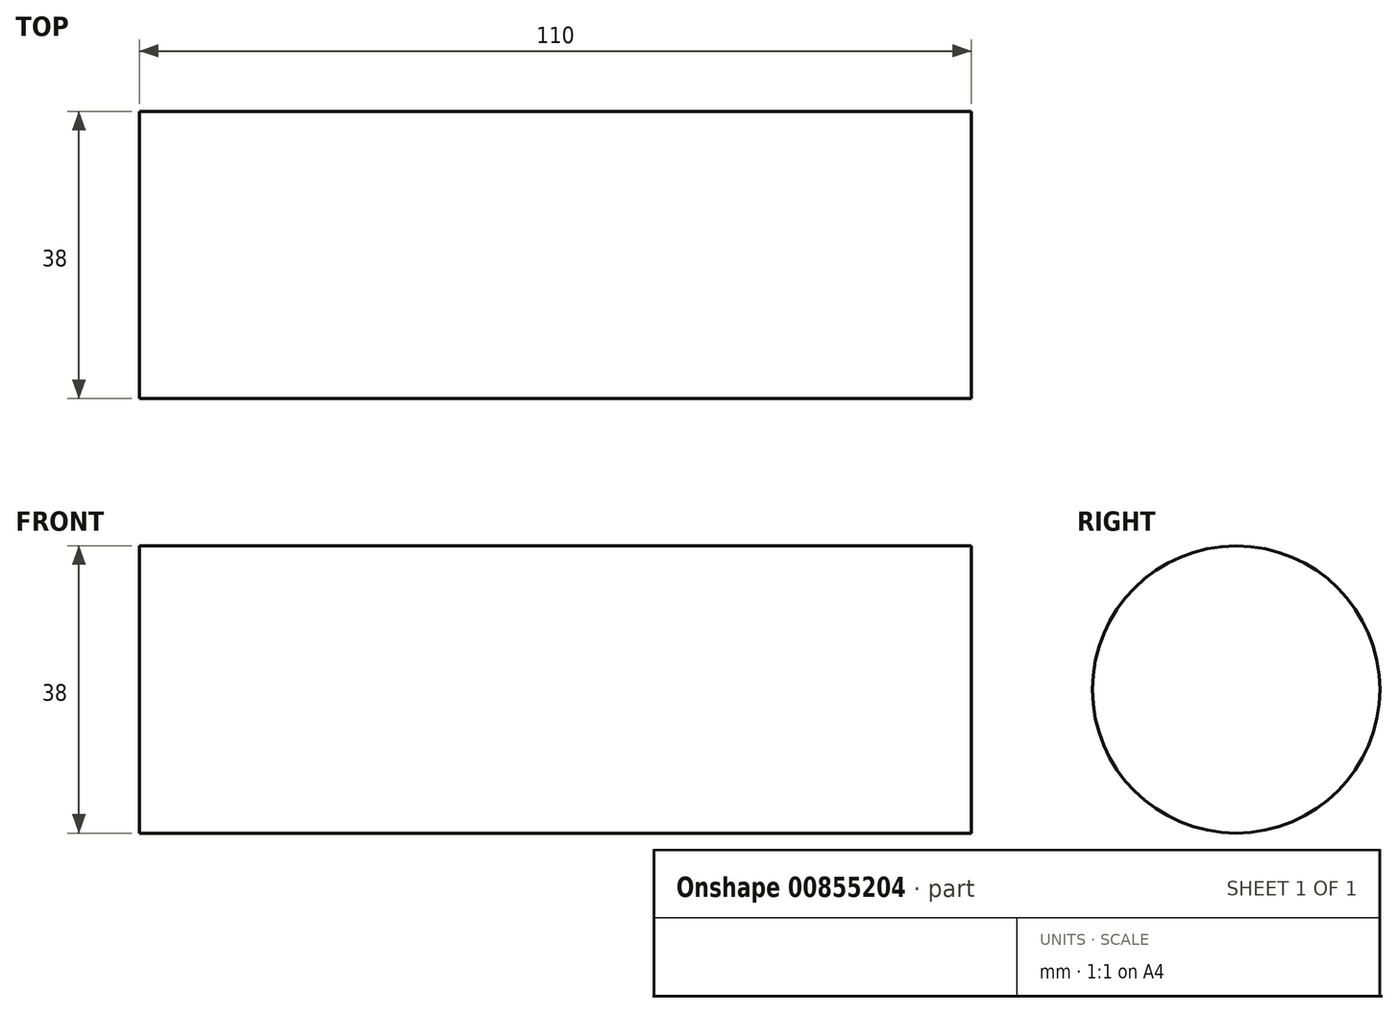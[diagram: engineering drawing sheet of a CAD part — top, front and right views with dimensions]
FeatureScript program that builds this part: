
annotation { "Feature Type Name" : "Feature", "Feature Type Description" : "" }
export const myFeature = defineFeature(function(context is Context, id is Id, definition is map)
    precondition{}
    {
        {
            var Q0;
            Q0=qCreatedBy(makeId("Right.planeOp"),FACE);
            var sketch = newSketch(context, id + "F0", { "sketchPlane" : qUnion([Q0])});
            skCircle(sketch, "E0", {"center": v(0, 0) * mm, "radius": 19 * mm});
            skSolve(sketch);
        }
        {
            var Q0;
            Q0=qSketchRegion(id+"F0",true);
            extrude(context, id + "F1", {"entities" : qUnion([Q0]), "depth" : 110 * mm, "offsetDistance" : 25 * mm});
        }
    });
